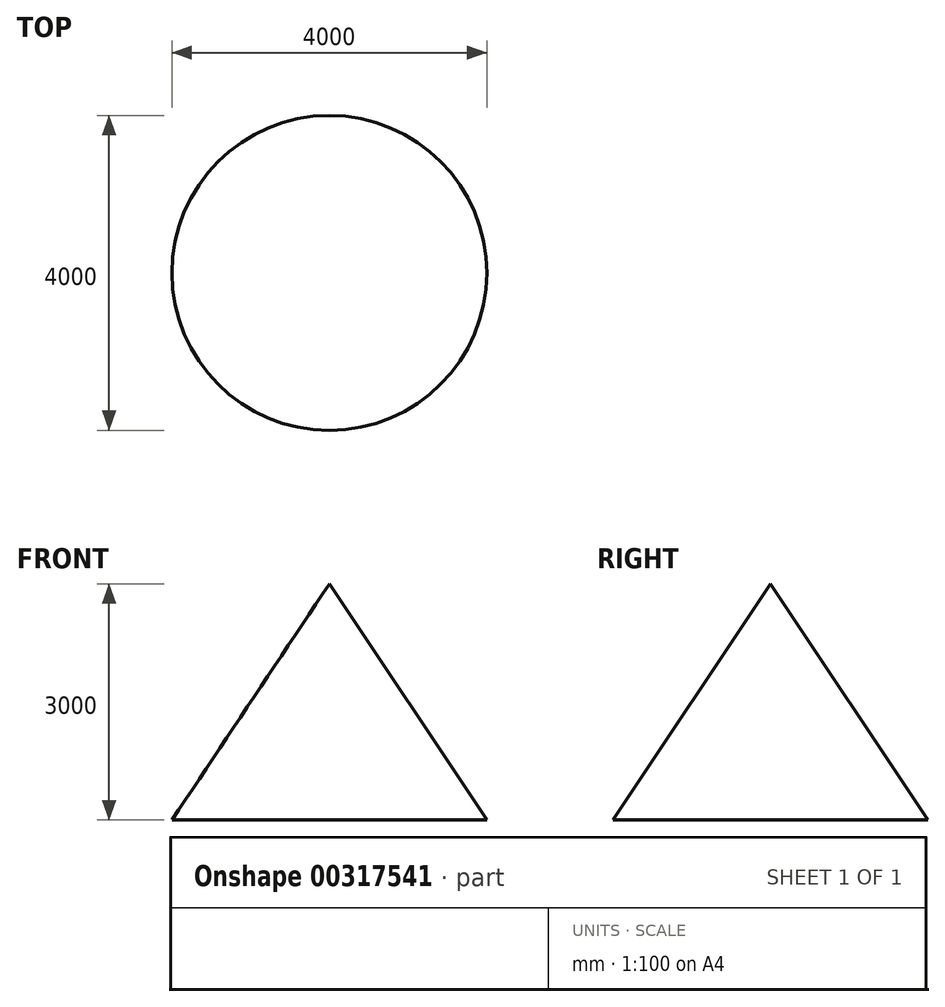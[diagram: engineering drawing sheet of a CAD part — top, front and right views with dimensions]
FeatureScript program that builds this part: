
annotation { "Feature Type Name" : "Feature", "Feature Type Description" : "" }
export const myFeature = defineFeature(function(context is Context, id is Id, definition is map)
    precondition{}
    {
        {
            var Q0;
            Q0=qCreatedBy(makeId("Front.planeOp"),FACE);
            var sketch = newSketch(context, id + "F0", { "sketchPlane" : qUnion([Q0])});
            skLineSegment(sketch, "E0", {"start": v(0, 0) * mm, "end": v(0, 3000) * mm});
            skLineSegment(sketch, "E1", {"start": v(0, 0) * mm, "end": v(2000, 0) * mm});
            skLineSegment(sketch, "E2", {"start": v(2000, 0) * mm, "end": v(0, 3000) * mm});
            skSolve(sketch);
        }
        {
            var Q0;
            Q0=makeQuery(id+"F0.imprint","IMPRINT",FACE,{"disambiguationData":[TD([[makeQuery(id+"F0.imprint","IMPRINT",EDGE,{"derivedFrom":sQuery(id+"F0.wireOp",EDGE,"E0")}),-1.0]])]});
            var Q1;
            Q1=sQuery(id+"F0.wireOp",EDGE,"E0");
            revolve(context, id + "F1", {"entities" : qUnion([Q0]), "axis" : qUnion([Q1]), "revolveType" : RevolveType.FULL});
        }
    });
